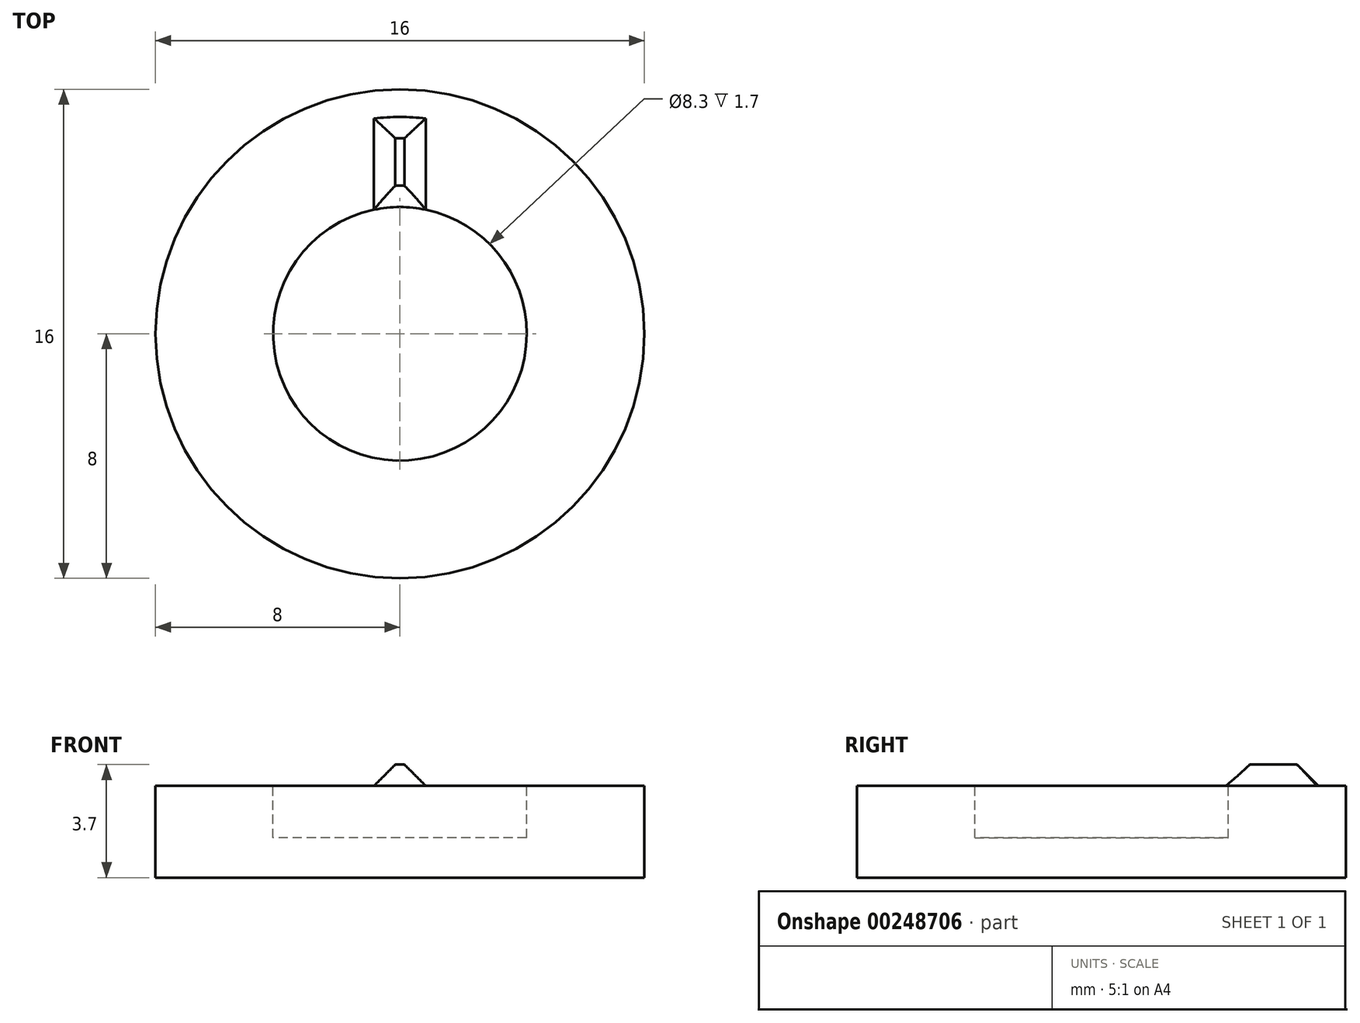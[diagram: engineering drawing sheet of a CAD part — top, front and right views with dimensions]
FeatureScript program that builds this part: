
annotation { "Feature Type Name" : "Feature", "Feature Type Description" : "" }
export const myFeature = defineFeature(function(context is Context, id is Id, definition is map)
    precondition{}
    {
        {
            var Q0;
            Q0=qCreatedBy(makeId("Top.planeOp"),FACE);
            var sketch = newSketch(context, id + "F0", { "sketchPlane" : qUnion([Q0])});
            skCircle(sketch, "E0", {"center": v(0, 0) * mm, "radius": 8 * mm});
            skSolve(sketch);
        }
        {
            var Q0;
            Q0 = qSketchRegion(id + "F0", true);
            extrude(context, id + "F1", {"entities" : qUnion([Q0]), "depth" : 3 * mm});
        }
        {
            var Q0;
            Q0=makeQuery(id+"F1.opExtrude","CAP_FACE",FACE,{"disambiguationData":[OSD([sQuery(id+"F0.wireOp",EDGE,"E0")])],"isStart":false});
            var sketch = newSketch(context, id + "F2", { "sketchPlane" : qUnion([Q0])});
            skCircle(sketch, "E1", {"center": v(0, 0) * mm, "radius": 4.15 * mm});
            skSolve(sketch);
        }
        {
            var Q0;
            Q0 = qSketchRegion(id + "F2", true);
            extrude(context, id + "F3", {"entities" : qUnion([Q0]), "operationType" : NewBodyOperationType.REMOVE, "oppositeDirection" : true, "depth" : 1.7 * mm});
        }
        {
            var Q0;
            Q0=makeQuery(id+"F1.opExtrude","CAP_FACE",FACE,{"disambiguationData":[OSD([sQuery(id+"F0.wireOp",EDGE,"E0")])],"isStart":false});
            var sketch = newSketch(context, id + "F4", { "sketchPlane" : qUnion([Q0])});
            skCircle(sketch, "E2", {"center": v(0, 0) * mm, "radius": 7.2 * mm});
            skLineSegment(sketch, "E3.bottom", {"start": v(0.95, 2.94) * mm, "end": v(-0.95, 2.94) * mm});
            skLineSegment(sketch, "E3.top", {"start": v(0.95, 11.46) * mm, "end": v(-0.95, 11.46) * mm});
            skLineSegment(sketch, "E3.left", {"start": v(0.95, 2.94) * mm, "end": v(0.95, 11.46) * mm});
            skLineSegment(sketch, "E3.right", {"start": v(-0.95, 2.94) * mm, "end": v(-0.95, 11.46) * mm});
            skPoint(sketch, "E3.middle", {"position": v(0, 7.2) * mm});
            skSolve(sketch);
        }
        {
            var Q0;
            {var subQ0=sQuery(id+"F4.wireOp",EDGE,"E3.left");var subQ1=sQuery(id+"F4.wireOp",EDGE,"E2");var subQ2=makeQuery(id+"F4.imprint","INTERSECT",VERTEX,{"derivedFrom":[subQ1,subQ0]});Q0=makeQuery(id+"F4.imprint","IMPRINT",FACE,{"disambiguationData":[TD([[makeQuery(id+"F4.imprint","IMPRINT",EDGE,{"disambiguationData":[TD([[subQ2,-1.0]])],"derivedFrom":subQ1}),1.0]])]});}
            extrude(context, id + "F5", {"entities" : qUnion([Q0]), "operationType" : NewBodyOperationType.ADD, "depth" : 0.7 * mm});
        }
        {
            var Q0;
            Q0=makeQuery(id+"F5.opExtrude","CAP_EDGE",EDGE,{"disambiguationData":[OSD([sQuery(id+"F4.wireOp",EDGE,"E3.left")])],"isStart":false});
            var Q1;
            Q1=makeQuery(id+"F5.opExtrude","CAP_EDGE",EDGE,{"disambiguationData":[OSD([sQuery(id+"F4.wireOp",EDGE,"E3.right")])],"isStart":false});
            chamfer(context, id + "F6", {"entities" : qUnion([Q0, Q1]), "width" : 0.8 * mm, "tangentPropagation" : true});
        }
        {
            var Q0;
            Q0=makeQuery(id+"F5.opExtrude","CAP_EDGE",EDGE,{"disambiguationData":[OSD([sQuery(id+"F4.wireOp",EDGE,"E2")])],"isStart":false});
            chamfer(context, id + "F7", {"entities" : qUnion([Q0]), "width" : 0.8 * mm, "tangentPropagation" : true});
        }
        {
            var Q0;
            Q0=makeQuery(id+"F5.opExtrude","CAP_EDGE",EDGE,{"disambiguationData":[OSD([sQuery(id+"F2.wireOp",EDGE,"E1")])],"isStart":false});
            chamfer(context, id + "F8", {"entities" : qUnion([Q0]), "width" : 0.7 * mm, "tangentPropagation" : true});
        }
    });
